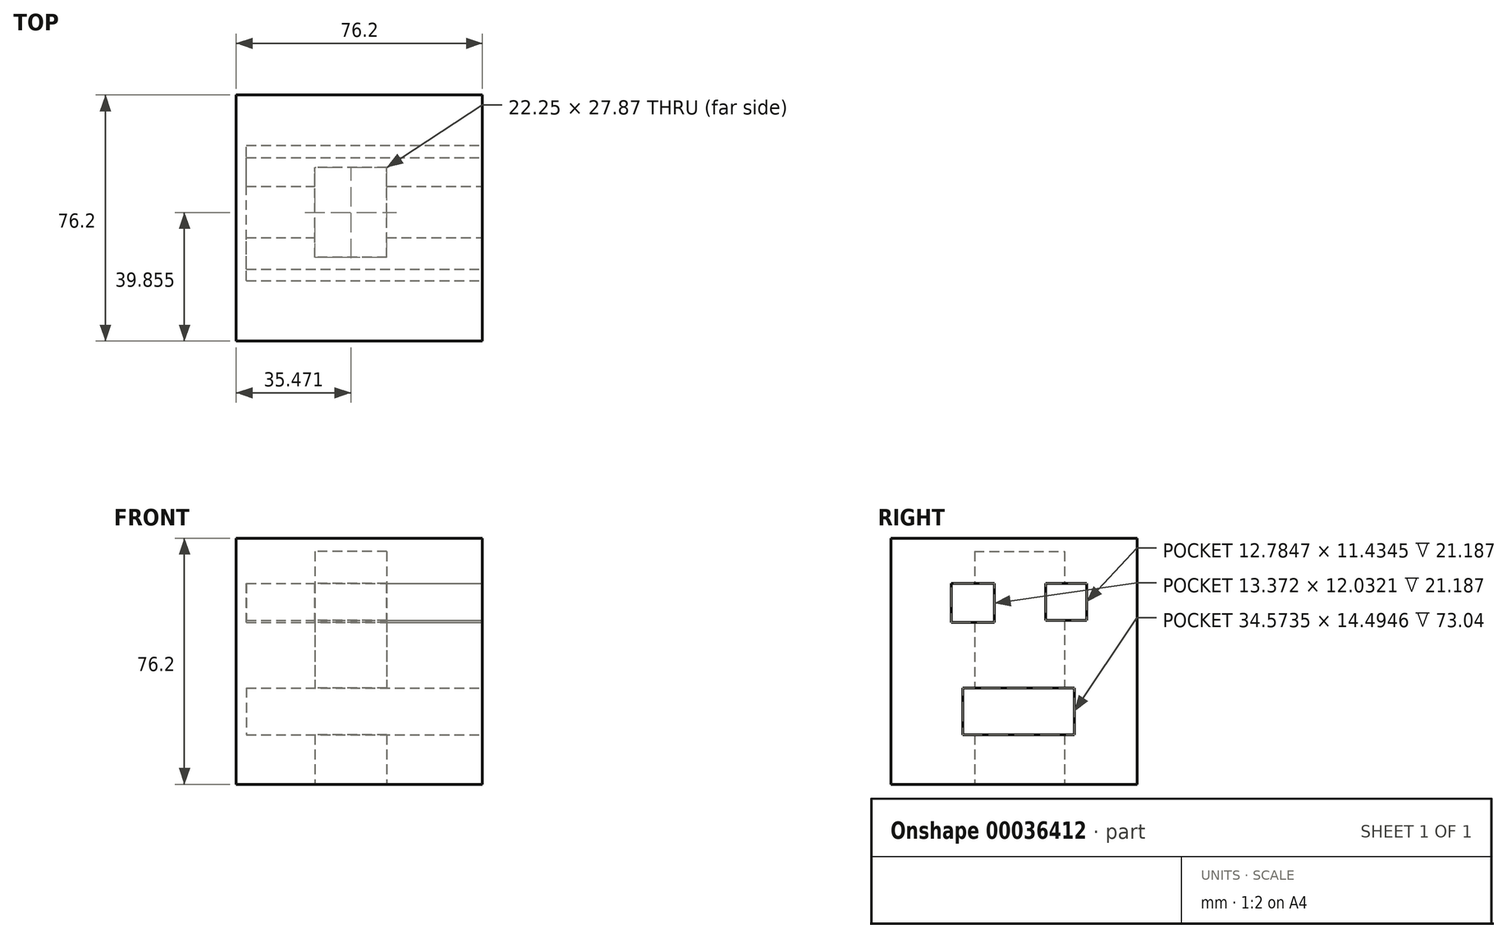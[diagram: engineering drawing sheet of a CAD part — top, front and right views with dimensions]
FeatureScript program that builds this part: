
annotation { "Feature Type Name" : "Feature", "Feature Type Description" : "" }
export const myFeature = defineFeature(function(context is Context, id is Id, definition is map)
    precondition{}
    {
        {
            var Q0;
            Q0=qCreatedBy(makeId("Front.planeOp"),FACE);
            var sketch = newSketch(context, id + "F0", { "sketchPlane" : qUnion([Q0])});
            skLineSegment(sketch, "E0.bottom", {"start": v(0, 0) * mm, "end": v(76.2, 0) * mm});
            skLineSegment(sketch, "E0.top", {"start": v(0, -76.2) * mm, "end": v(76.2, -76.2) * mm});
            skLineSegment(sketch, "E0.left", {"start": v(0, 0) * mm, "end": v(0, -76.2) * mm});
            skLineSegment(sketch, "E0.right", {"start": v(76.2, 0) * mm, "end": v(76.2, -76.2) * mm});
            skSolve(sketch);
        }
        {
            var Q0;
            Q0=makeQuery(id+"F0.imprint","IMPRINT",FACE,{"disambiguationData":[TD([[makeQuery(id+"F0.imprint","IMPRINT",EDGE,{"derivedFrom":sQuery(id+"F0.wireOp",EDGE,"E0.bottom")}),-1.0]])]});
            extrude(context, id + "F1", {"entities" : qUnion([Q0]), "depth" : 76.2 * mm});
        }
        {
            var Q0;
            Q0=makeQuery(id+"F1.opExtrude","SWEPT_FACE",FACE,{"disambiguationData":[OSD([sQuery(id+"F0.wireOp",EDGE,"E0.right")])]});
            var sketch = newSketch(context, id + "F2", { "sketchPlane" : qUnion([Q0])});
            skLineSegment(sketch, "E1.bottom", {"start": v(-57.47, -26.1) * mm, "end": v(-44.1, -26.1) * mm});
            skLineSegment(sketch, "E1.top", {"start": v(-57.47, -14.07) * mm, "end": v(-44.1, -14.07) * mm});
            skLineSegment(sketch, "E1.left", {"start": v(-57.47, -26.1) * mm, "end": v(-57.47, -14.07) * mm});
            skLineSegment(sketch, "E1.right", {"start": v(-44.1, -26.1) * mm, "end": v(-44.1, -14.07) * mm});
            skLineSegment(sketch, "E2.bottom", {"start": v(-28.3, -14.03) * mm, "end": v(-15.52, -14.03) * mm});
            skLineSegment(sketch, "E2.top", {"start": v(-28.3, -25.47) * mm, "end": v(-15.52, -25.47) * mm});
            skLineSegment(sketch, "E2.left", {"start": v(-28.3, -14.03) * mm, "end": v(-28.3, -25.47) * mm});
            skLineSegment(sketch, "E2.right", {"start": v(-15.52, -14.03) * mm, "end": v(-15.52, -25.47) * mm});
            skLineSegment(sketch, "E3.bottom", {"start": v(-53.94, -46.37) * mm, "end": v(-19.37, -46.37) * mm});
            skLineSegment(sketch, "E3.top", {"start": v(-53.94, -60.87) * mm, "end": v(-19.37, -60.87) * mm});
            skLineSegment(sketch, "E3.left", {"start": v(-53.94, -46.37) * mm, "end": v(-53.94, -60.87) * mm});
            skLineSegment(sketch, "E3.right", {"start": v(-19.37, -46.37) * mm, "end": v(-19.37, -60.87) * mm});
            skSolve(sketch);
        }
        {
            var Q0;
            Q0=makeQuery(id+"F1.opExtrude","SWEPT_FACE",FACE,{"disambiguationData":[OSD([sQuery(id+"F0.wireOp",EDGE,"E0.top")])]});
            var sketch = newSketch(context, id + "F3", { "sketchPlane" : qUnion([Q0])});
            skLineSegment(sketch, "E4.bottom", {"start": v(46.6, 50.28) * mm, "end": v(24.35, 50.28) * mm});
            skLineSegment(sketch, "E4.top", {"start": v(46.6, 22.41) * mm, "end": v(24.35, 22.41) * mm});
            skLineSegment(sketch, "E4.left", {"start": v(46.6, 50.28) * mm, "end": v(46.6, 22.41) * mm});
            skLineSegment(sketch, "E4.right", {"start": v(24.35, 50.28) * mm, "end": v(24.35, 22.41) * mm});
            skSolve(sketch);
        }
        {
            var Q0;
            Q0=makeQuery(id+"F2.imprint","IMPRINT",FACE,{"disambiguationData":[TD([[makeQuery(id+"F2.imprint","IMPRINT",EDGE,{"derivedFrom":sQuery(id+"F2.wireOp",EDGE,"E2.bottom")}),-1.0]])]});
            var Q1;
            Q1=makeQuery(id+"F2.imprint","IMPRINT",FACE,{"disambiguationData":[TD([[makeQuery(id+"F2.imprint","IMPRINT",EDGE,{"derivedFrom":sQuery(id+"F2.wireOp",EDGE,"E1.bottom")}),1.0]])]});
            var Q2;
            Q2=makeQuery(id+"F2.imprint","IMPRINT",FACE,{"disambiguationData":[TD([[makeQuery(id+"F2.imprint","IMPRINT",EDGE,{"derivedFrom":sQuery(id+"F2.wireOp",EDGE,"E3.bottom")}),-1.0]])]});
            extrude(context, id + "F4", {"entities" : qUnion([Q0, Q1, Q2]), "operationType" : NewBodyOperationType.REMOVE, "oppositeDirection" : true, "depth" : 73.04 * mm});
        }
        {
            var Q0;
            Q0=makeQuery(id+"F3.imprint","IMPRINT",FACE,{"disambiguationData":[TD([[makeQuery(id+"F3.imprint","IMPRINT",EDGE,{"derivedFrom":sQuery(id+"F3.wireOp",EDGE,"E4.bottom")}),1.0]])]});
            extrude(context, id + "F5", {"entities" : qUnion([Q0]), "operationType" : NewBodyOperationType.REMOVE, "oppositeDirection" : true, "depth" : 72.06 * mm});
        }
    });
